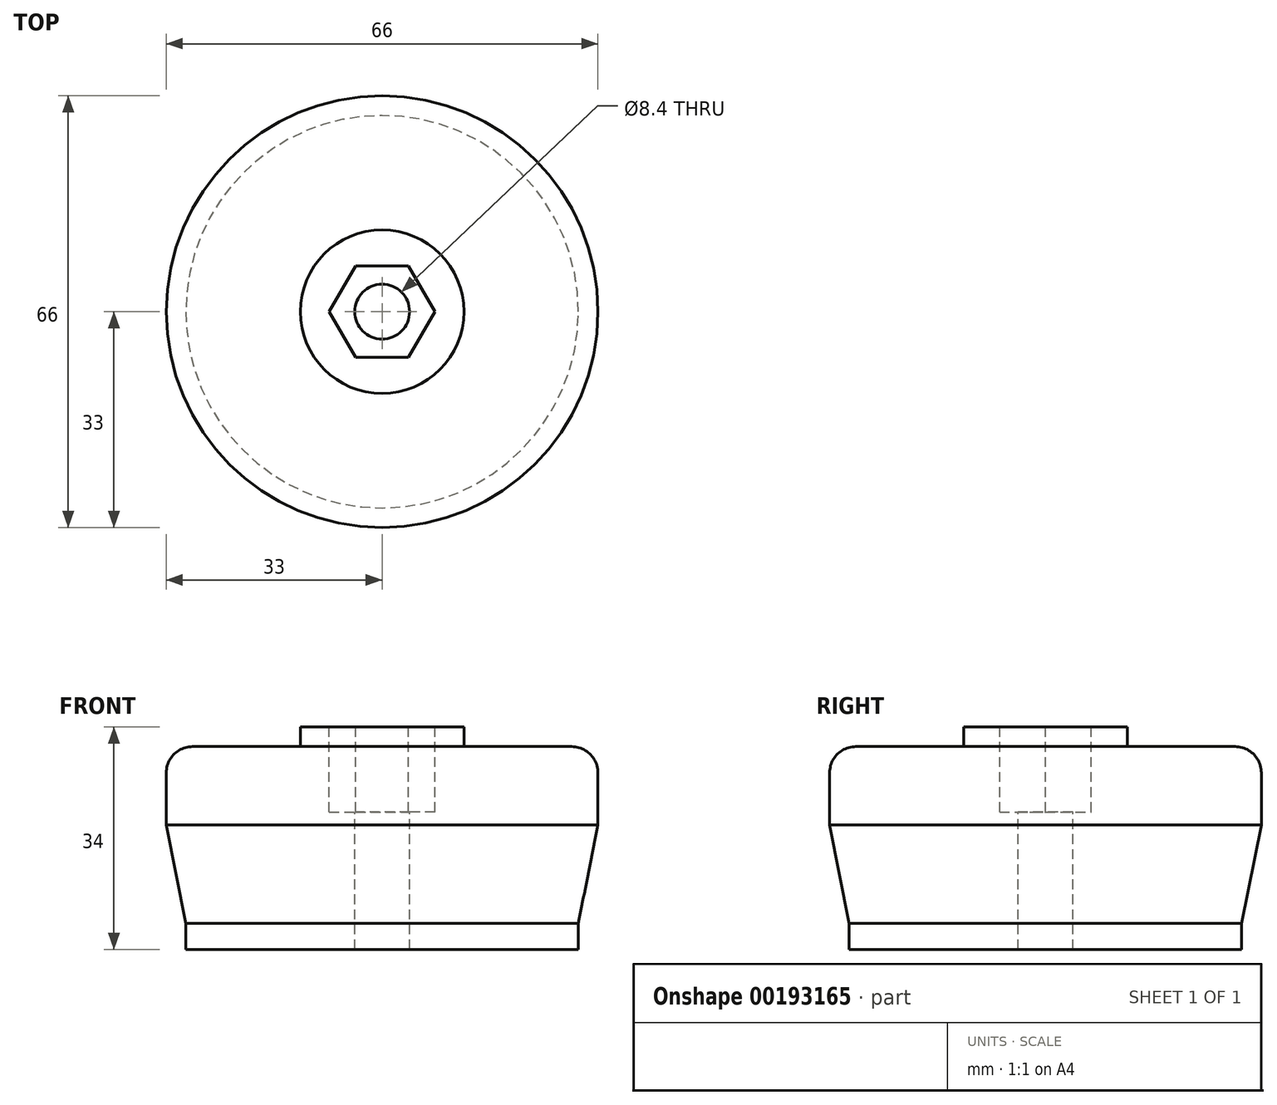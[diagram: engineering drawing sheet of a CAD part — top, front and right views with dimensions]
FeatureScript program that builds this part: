
annotation { "Feature Type Name" : "Feature", "Feature Type Description" : "" }
export const myFeature = defineFeature(function(context is Context, id is Id, definition is map)
    precondition{}
    {
        {
            var Q0;
            Q0=qCreatedBy(makeId("Top.planeOp"),FACE);
            var sketch = newSketch(context, id + "F0", { "sketchPlane" : qUnion([Q0])});
            skCircle(sketch, "E0", {"center": v(0, 0) * mm, "radius": 33 * mm});
            skSolve(sketch);
        }
        {
            var Q0;
            Q0=makeQuery(id+"F0.imprint","IMPRINT",FACE,{"disambiguationData":[TD([[makeQuery(id+"F0.imprint","IMPRINT",EDGE,{"derivedFrom":sQuery(id+"F0.wireOp",EDGE,"E0")}),1.0]])]});
            extrude(context, id + "F1", {"entities" : qUnion([Q0]), "depth" : 12 * mm});
        }
        {
            var Q0;
            Q0=makeQuery(id+"F1.opExtrude","CAP_FACE",FACE,{"disambiguationData":[OSD([sQuery(id+"F0.wireOp",EDGE,"E0")])],"isStart":false});
            var sketch = newSketch(context, id + "F2", { "sketchPlane" : qUnion([Q0])});
            skCircle(sketch, "E1.cCircle", {"center": v(0, 0) * mm, "radius": 7 * mm, "construction": true});
            skLineSegment(sketch, "E1.0", {"start": v(-4.04, 7) * mm, "end": v(4.04, 7) * mm});
            skLineSegment(sketch, "E1.1", {"start": v(4.04, 7) * mm, "end": v(8.08, 0) * mm});
            skLineSegment(sketch, "E1.2", {"start": v(8.08, 0) * mm, "end": v(4.04, -7) * mm});
            skLineSegment(sketch, "E1.3", {"start": v(4.04, -7) * mm, "end": v(-4.04, -7) * mm});
            skLineSegment(sketch, "E1.4", {"start": v(-4.04, -7) * mm, "end": v(-8.08, 0) * mm});
            skLineSegment(sketch, "E1.5", {"start": v(-8.08, 0) * mm, "end": v(-4.04, 7) * mm});
            skPoint(sketch, "E1.0.midPoint", {"position": v(0, 7) * mm});
            skCircle(sketch, "E2", {"center": v(0, 0) * mm, "radius": 12.5 * mm});
            skSolve(sketch);
        }
        {
            var Q0;
            Q0=makeQuery(id+"F2.imprint","IMPRINT",FACE,{"disambiguationData":[TD([[makeQuery(id+"F2.imprint","IMPRINT",EDGE,{"derivedFrom":sQuery(id+"F2.wireOp",EDGE,"E1.0")}),-1.0]])]});
            extrude(context, id + "F3", {"entities" : qUnion([Q0]), "operationType" : NewBodyOperationType.REMOVE, "oppositeDirection" : true, "depth" : 10 * mm});
        }
        {
            var Q0;
            Q0=makeQuery(id+"F2.imprint","IMPRINT",FACE,{"disambiguationData":[TD([[makeQuery(id+"F2.imprint","IMPRINT",EDGE,{"derivedFrom":sQuery(id+"F2.wireOp",EDGE,"E1.0")}),1.0]])]});
            extrude(context, id + "F4", {"entities" : qUnion([Q0]), "operationType" : NewBodyOperationType.ADD, "depth" : 3 * mm});
        }
        {
            var Q0;
            Q0=makeQuery(id+"F1.opExtrude","CAP_EDGE",EDGE,{"disambiguationData":[OSD([sQuery(id+"F0.wireOp",EDGE,"E0")])],"isStart":false});
            fillet(context, id + "F5", {"entities" : qUnion([Q0]), "radius" : 4 * mm, "tangentPropagation" : true, "allowEdgeOverflow" : false});
        }
        {
            var Q0;
            Q0=sQuery(id+"F2.wireOp",VERTEX,"E1.cCircle.center");
            var Q1;
            Q1=makeQuery(id+"F1.opExtrude","SWEPT_BODY",BODY,{"disambiguationData":[OSD([sQuery(id+"F0.wireOp",EDGE,"E0")])]});
            hole(context, id + "F6", {"style" : HoleStyle.SIMPLE, "endStyle" : HoleEndStyle.BLIND, "standardTappedOrClearance" : lookupTablePath({ "standard" : "ISO", "fit" : "Close", "size" : "M8", "type" : "Clearance" }), "standardBlindInLast" : lookupTablePath({ "fit" : "Close", "standard" : "ISO", "size" : "M8", "type" : "Clearance" }), "holeDiameter" : 8.4 * mm, "holeDepth" : 12 * mm, "locations" : qUnion([Q0]), "scope" : qUnion([Q1])});
        }
        {
            var Q0;
            Q0=makeQuery(id+"F1.opExtrude","CAP_FACE",FACE,{"disambiguationData":[OSD([sQuery(id+"F0.wireOp",EDGE,"E0")])],"isStart":true});
            extrude(context, id + "F7", {"entities" : qUnion([Q0]), "operationType" : NewBodyOperationType.ADD, "depth" : 15 * mm});
        }
        {
            var Q0;
            Q0=makeQuery(id+"F7.opExtrude","CAP_EDGE",EDGE,{"disambiguationData":[OSD([sQuery(id+"F0.wireOp",EDGE,"E0")])],"isStart":false});
            chamfer(context, id + "F8", {"entities" : qUnion([Q0]), "chamferType" : ChamferType.TWO_OFFSETS, "width1" : 15 * mm, "oppositeDirection" : false, "width2" : 3 * mm, "tangentPropagation" : true});
        }
        {
            var Q0;
            Q0=makeQuery(id+"F7.opExtrude","CAP_FACE",FACE,{"disambiguationData":[OSD([sQuery(id+"F0.wireOp",EDGE,"E0")])],"isStart":false});
            var sketch = newSketch(context, id + "F9", { "sketchPlane" : qUnion([Q0])});
            skCircle(sketch, "E3.0", {"center": v(0, 0) * mm, "radius": 12.7 * mm});
            skSolve(sketch);
        }
        {
            var Q0;
            Q0=makeQuery(id+"F9.imprint","IMPRINT",FACE,{"disambiguationData":[TD([[makeQuery(id+"F9.imprint","IMPRINT",EDGE,{"derivedFrom":sQuery(id+"F9.wireOp",EDGE,"E3.0")}),-1.0]])]});
            var Q1;
            Q1=makeQuery(id+"F9.imprint","IMPRINT",FACE,{"disambiguationData":[TD([[makeQuery(id+"F9.imprint","IMPRINT",EDGE,{"derivedFrom":sQuery(id+"F9.wireOp",EDGE,"E3.0")}),1.0]])]});
            extrude(context, id + "F10", {"entities" : qUnion([Q0, Q1]), "operationType" : NewBodyOperationType.ADD, "depth" : 4 * mm});
        }
    });
